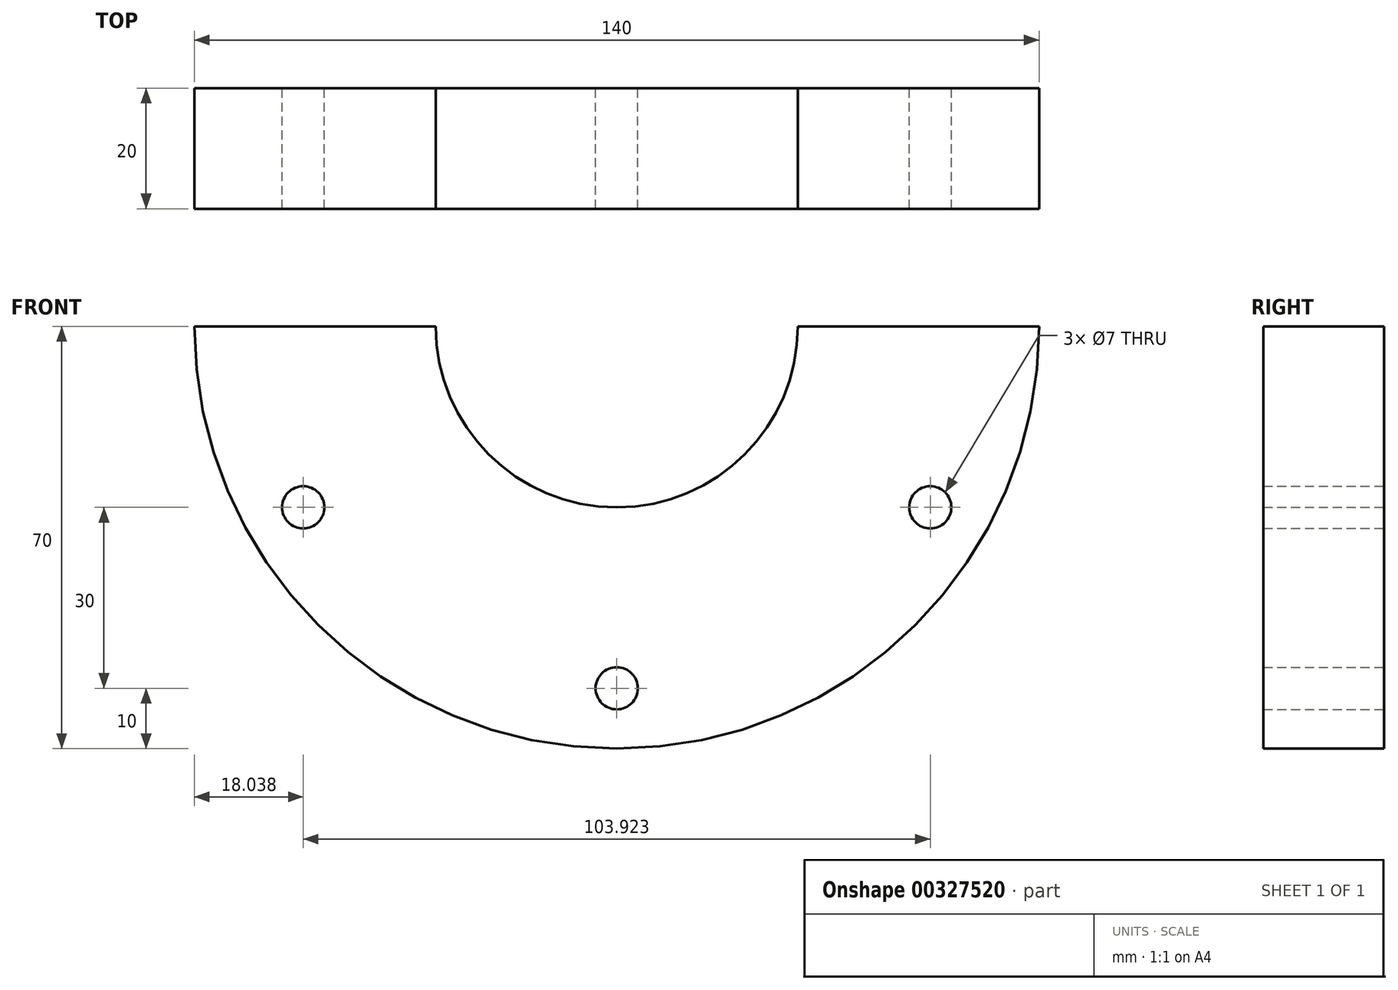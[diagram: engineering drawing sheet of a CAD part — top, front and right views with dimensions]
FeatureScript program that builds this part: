
annotation { "Feature Type Name" : "Feature", "Feature Type Description" : "" }
export const myFeature = defineFeature(function(context is Context, id is Id, definition is map)
    precondition{}
    {
        {
            var Q0;
            Q0=qCreatedBy(makeId("Front.planeOp"),FACE);
            var sketch = newSketch(context, id + "F0", { "sketchPlane" : qUnion([Q0])});
            skLineSegment(sketch, "E0", {"start": v(70, 0) * mm, "end": v(30, 0) * mm});
            skArc(sketch, "E1", {"start": v(-70, 0) * mm, "mid": v(0, -70) * mm, "end": v(70, 0) * mm});
            skCircle(sketch, "E2.MirrorC", {"center": v(-51.96, -30) * mm, "radius": 3.5 * mm});
            skArc(sketch, "E3", {"start": v(-60, 0) * mm, "mid": v(0, -60) * mm, "end": v(60, 0) * mm, "construction": true});
            skArc(sketch, "E4", {"start": v(-30, 0) * mm, "mid": v(0, -30) * mm, "end": v(30, 0) * mm});
            skLineSegment(sketch, "E5", {"start": v(0, 0) * mm, "end": v(0, -70) * mm, "construction": true});
            skCircle(sketch, "E6", {"center": v(0, -60) * mm, "radius": 3.5 * mm});
            skCircle(sketch, "E7.1.0", {"center": v(51.96, -30) * mm, "radius": 3.5 * mm});
            skLineSegment(sketch, "E8.trimOffspring", {"start": v(-30, 0) * mm, "end": v(-70, 0) * mm});
            skSolve(sketch);
        }
        {
            var Q0;
            Q0 = qSketchRegion(id + "F0", true);
            extrude(context, id + "F1", {"entities" : qUnion([Q0]), "depth" : 20 * mm});
        }
    });
